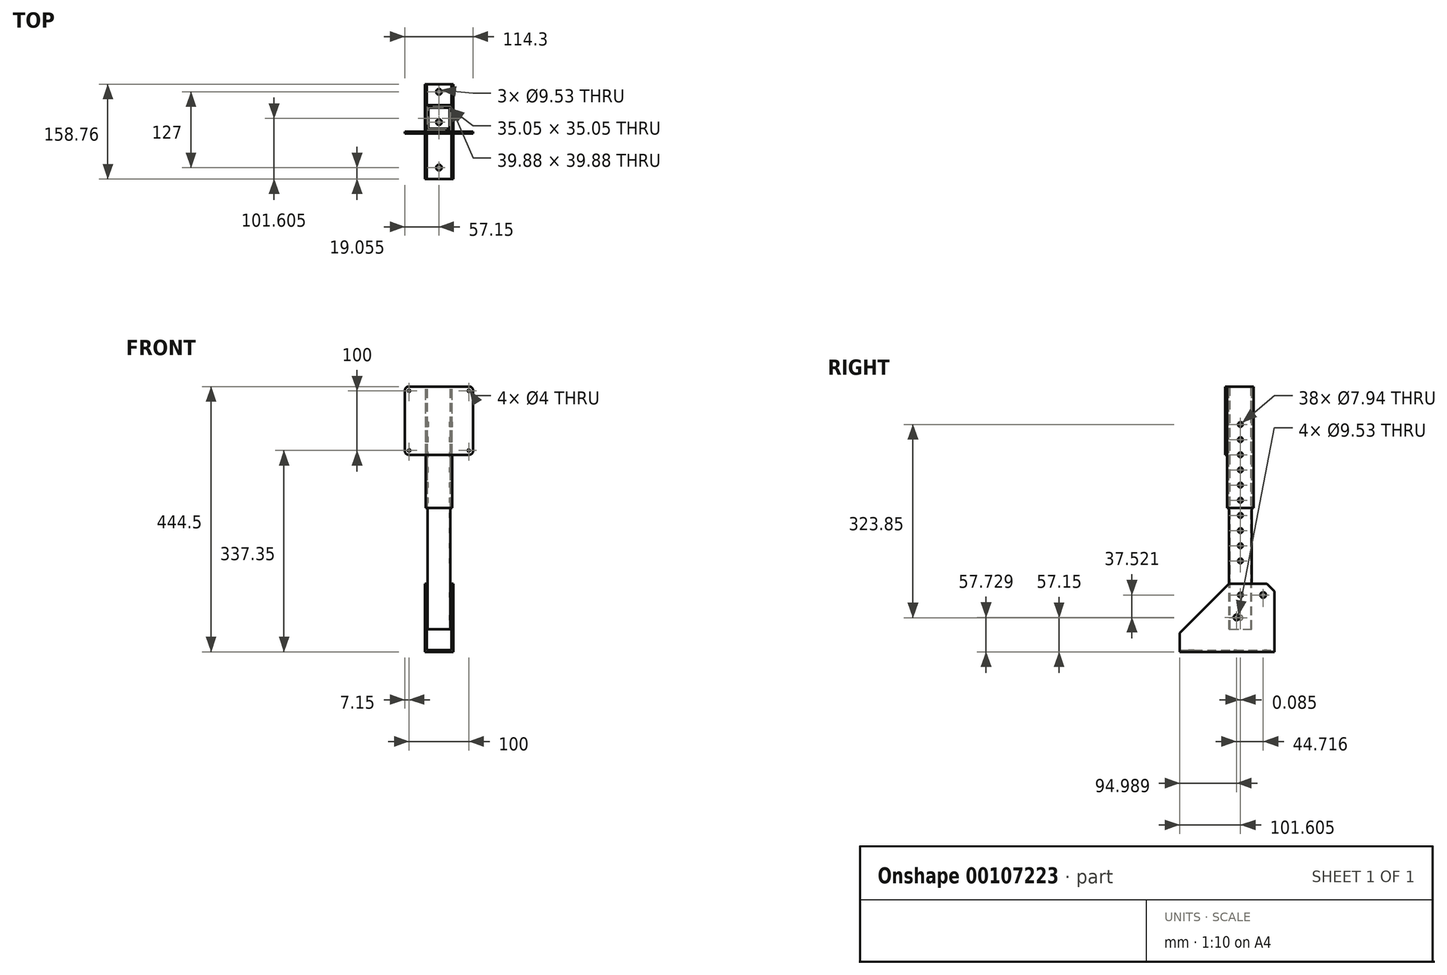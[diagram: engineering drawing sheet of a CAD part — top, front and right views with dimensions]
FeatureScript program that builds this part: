
annotation { "Feature Type Name" : "Feature", "Feature Type Description" : "" }
export const myFeature = defineFeature(function(context is Context, id is Id, definition is map)
    precondition{}
    {
        {
            var Q0;
            Q0=qCreatedBy(makeId("Front.planeOp"),FACE);
            var sketch = newSketch(context, id + "F0", { "sketchPlane" : qUnion([Q0])});
            skLineSegment(sketch, "E0.bottom", {"start": v(50, 50) * mm, "end": v(-50, 50) * mm, "construction": true});
            skLineSegment(sketch, "E0.top", {"start": v(50, -50) * mm, "end": v(-50, -50) * mm, "construction": true});
            skLineSegment(sketch, "E0.left", {"start": v(50, 50) * mm, "end": v(50, -50) * mm, "construction": true});
            skLineSegment(sketch, "E0.right", {"start": v(-50, 50) * mm, "end": v(-50, -50) * mm, "construction": true});
            skPoint(sketch, "E0.middle", {"position": v(0, 0) * mm});
            skCircle(sketch, "E1", {"center": v(-50, 50) * mm, "radius": 2 * mm});
            skCircle(sketch, "E2", {"center": v(50, 50) * mm, "radius": 2 * mm});
            skCircle(sketch, "E3", {"center": v(50, -50) * mm, "radius": 2 * mm});
            skCircle(sketch, "E4", {"center": v(-50, -50) * mm, "radius": 2 * mm});
            skLineSegment(sketch, "E5.bottom", {"start": v(57.15, 57.15) * mm, "end": v(-57.15, 57.15) * mm});
            skLineSegment(sketch, "E5.top", {"start": v(57.15, -57.15) * mm, "end": v(-57.15, -57.15) * mm});
            skLineSegment(sketch, "E5.left", {"start": v(57.15, 57.15) * mm, "end": v(57.15, -57.15) * mm});
            skLineSegment(sketch, "E5.right", {"start": v(-57.15, 57.15) * mm, "end": v(-57.15, -57.15) * mm});
            skSolve(sketch);
        }
        {
            var Q0;
            Q0=makeQuery(id+"F0.imprint","IMPRINT",FACE,{"disambiguationData":[TD([[makeQuery(id+"F0.imprint","IMPRINT",EDGE,{"derivedFrom":sQuery(id+"F0.wireOp",EDGE,"E1")}),-1.0]])]});
            extrude(context, id + "F1", {"entities" : qUnion([Q0]), "depth" : 3.17 * mm});
        }
        {
            var Q0;
            Q0=makeQuery(id+"F1.opExtrude","SWEPT_EDGE",EDGE,{"disambiguationData":[OSD([sQuery(id+"F0.wireOp",EDGE,"E5.bottom"),sQuery(id+"F0.wireOp",EDGE,"E5.right")])]});
            var Q1;
            Q1=makeQuery(id+"F1.opExtrude","SWEPT_EDGE",EDGE,{"disambiguationData":[OSD([sQuery(id+"F0.wireOp",EDGE,"E5.bottom"),sQuery(id+"F0.wireOp",EDGE,"E5.left")])]});
            var Q2;
            Q2=makeQuery(id+"F1.opExtrude","SWEPT_EDGE",EDGE,{"disambiguationData":[OSD([sQuery(id+"F0.wireOp",EDGE,"E5.top"),sQuery(id+"F0.wireOp",EDGE,"E5.right")])]});
            var Q3;
            Q3=makeQuery(id+"F1.opExtrude","SWEPT_EDGE",EDGE,{"disambiguationData":[OSD([sQuery(id+"F0.wireOp",EDGE,"E5.top"),sQuery(id+"F0.wireOp",EDGE,"E5.left")])]});
            fillet(context, id + "F2", {"entities" : qUnion([Q0, Q1, Q2, Q3]), "radius" : 6.35 * mm, "tangentPropagation" : true, "allowEdgeOverflow" : false});
        }
        {
            var Q0;
            Q0=makeQuery(id+"F1.opExtrude","SWEPT_FACE",FACE,{"disambiguationData":[OSD([sQuery(id+"F0.wireOp",EDGE,"E5.bottom")])]});
            var sketch = newSketch(context, id + "F3", { "sketchPlane" : qUnion([Q0])});
            skLineSegment(sketch, "E6.bottom", {"start": v(-22.23, 0) * mm, "end": v(22.23, 0) * mm});
            skLineSegment(sketch, "E6.top", {"start": v(-22.23, 44.45) * mm, "end": v(22.23, 44.45) * mm});
            skLineSegment(sketch, "E6.left", {"start": v(-22.23, 0) * mm, "end": v(-22.23, 44.45) * mm});
            skLineSegment(sketch, "E6.right", {"start": v(22.23, 0) * mm, "end": v(22.23, 44.45) * mm});
            skLineSegment(sketch, "E7.0", {"start": v(-19.94, 42.16) * mm, "end": v(19.94, 42.16) * mm});
            skLineSegment(sketch, "E7.1", {"start": v(-19.94, 2.29) * mm, "end": v(-19.94, 42.16) * mm});
            skLineSegment(sketch, "E7.2", {"start": v(-19.94, 2.29) * mm, "end": v(19.94, 2.29) * mm});
            skLineSegment(sketch, "E7.3", {"start": v(19.94, 2.29) * mm, "end": v(19.94, 42.16) * mm});
            skSolve(sketch);
        }
        {
            var Q0;
            Q0=makeQuery(id+"F3.imprint","IMPRINT",FACE,{"disambiguationData":[TD([[makeQuery(id+"F3.imprint","IMPRINT",EDGE,{"derivedFrom":sQuery(id+"F3.wireOp",EDGE,"E6.bottom")}),-1.0]])]});
            extrude(context, id + "F4", {"entities" : qUnion([Q0]), "oppositeDirection" : true, "depth" : 203.2 * mm});
        }
        {
            var Q0;
            Q0=qCreatedBy(makeId("Front.planeOp"),FACE);
            var sketch = newSketch(context, id + "F5", { "sketchPlane" : qUnion([Q0])});
            skLineSegment(sketch, "E8.bottom", {"start": v(-254, -155.95) * mm, "end": v(254, -155.95) * mm});
            skLineSegment(sketch, "E8.top", {"start": v(-254, 148.85) * mm, "end": v(254, 148.85) * mm});
            skLineSegment(sketch, "E8.left", {"start": v(-254, -155.95) * mm, "end": v(-254, 148.85) * mm});
            skLineSegment(sketch, "E8.right", {"start": v(254, -155.95) * mm, "end": v(254, 148.85) * mm});
            skLineSegment(sketch, "E9.bottom", {"start": v(-457.2, -384.55) * mm, "end": v(457.2, -384.55) * mm});
            skLineSegment(sketch, "E9.top", {"start": v(-457.2, -397.25) * mm, "end": v(457.2, -397.25) * mm});
            skLineSegment(sketch, "E9.left", {"start": v(-457.2, -384.55) * mm, "end": v(-457.2, -397.25) * mm});
            skLineSegment(sketch, "E9.right", {"start": v(457.2, -384.55) * mm, "end": v(457.2, -397.25) * mm});
            skLineSegment(sketch, "E10", {"start": v(0, -155.95) * mm, "end": v(0, -384.55) * mm});
            skSolve(sketch);
        }
        {
            var Q0;
            Q0=qCreatedBy(makeId("Right.planeOp"),FACE);
            var sketch = newSketch(context, id + "F6", { "sketchPlane" : qUnion([Q0])});
            skLineSegment(sketch, "E11.bottom", {"start": v(3.18, -387.35) * mm, "end": v(79.38, -387.35) * mm});
            skLineSegment(sketch, "E11.top", {"start": v(3.18, -273.05) * mm, "end": v(79.38, -273.05) * mm});
            skLineSegment(sketch, "E11.left", {"start": v(3.18, -387.35) * mm, "end": v(3.18, -273.05) * mm, "construction": true});
            skLineSegment(sketch, "E11.right", {"start": v(79.38, -387.35) * mm, "end": v(79.38, -273.05) * mm});
            skCircle(sketch, "E12", {"center": v(22.23, -292.1) * mm, "radius": 3.97 * mm});
            skCircle(sketch, "E13", {"center": v(15.6, -329.62) * mm, "radius": 4.76 * mm});
            skCircle(sketch, "E14", {"center": v(60.33, -292.1) * mm, "radius": 4.76 * mm});
            skLineSegment(sketch, "E15", {"start": v(22.23, -292.1) * mm, "end": v(60.33, -292.1) * mm, "construction": true});
            skLineSegment(sketch, "E16", {"start": v(15.6, -329.62) * mm, "end": v(22.23, -292.1) * mm, "construction": true});
            skLineSegment(sketch, "E17", {"start": v(3.18, -387.35) * mm, "end": v(-79.37, -387.35) * mm});
            skLineSegment(sketch, "E18", {"start": v(-79.37, -387.35) * mm, "end": v(-79.37, -355.6) * mm});
            skLineSegment(sketch, "E19", {"start": v(-79.37, -355.6) * mm, "end": v(3.18, -273.05) * mm});
            skSolve(sketch);
        }
        {
            var Q0;
            Q0=makeQuery(id+"F6.imprint","IMPRINT",FACE,{"disambiguationData":[TD([[makeQuery(id+"F6.imprint","IMPRINT",EDGE,{"derivedFrom":sQuery(id+"F6.wireOp",EDGE,"E11.bottom")}),1.0]])]});
            extrude(context, id + "F7", {"entities" : qUnion([Q0]), "endBound" : BoundingType.SYMMETRIC, "depth" : 47.62 * mm});
        }
        {
            var Q0;
            Q0=makeQuery(id+"F7.opExtrude","SWEPT_FACE",FACE,{"disambiguationData":[OSD([sQuery(id+"F6.wireOp",EDGE,"E11.right")])]});
            var Q1;
            Q1=makeQuery(id+"F7.opExtrude","SWEPT_FACE",FACE,{"disambiguationData":[OSD([sQuery(id+"F6.wireOp",EDGE,"E11.top")])]});
            var Q2;
            Q2=makeQuery(id+"F7.opExtrude","SWEPT_FACE",FACE,{"disambiguationData":[OSD([sQuery(id+"F6.wireOp",EDGE,"E13")])]});
            var Q3;
            Q3=makeQuery(id+"F7.opExtrude","SWEPT_FACE",FACE,{"disambiguationData":[OSD([sQuery(id+"F6.wireOp",EDGE,"E12")])]});
            var Q4;
            Q4=makeQuery(id+"F7.opExtrude","SWEPT_FACE",FACE,{"disambiguationData":[OSD([sQuery(id+"F6.wireOp",EDGE,"E14")])]});
            var Q5;
            Q5=makeQuery(id+"F7.opExtrude","SWEPT_FACE",FACE,{"disambiguationData":[OSD([sQuery(id+"F6.wireOp",EDGE,"E18")])]});
            var Q6;
            Q6=makeQuery(id+"F7.opExtrude","SWEPT_FACE",FACE,{"disambiguationData":[OSD([sQuery(id+"F6.wireOp",EDGE,"E19")])]});
            shell(context, id + "F8", {"entities" : qUnion([Q0, Q1, Q2, Q3, Q4, Q5, Q6]), "thickness" : 3.17 * mm});
        }
        {
            var Q0;
            Q0=qCreatedBy(makeId("Right.planeOp"),FACE);
            var sketch = newSketch(context, id + "F9", { "sketchPlane" : qUnion([Q0])});
            skLineSegment(sketch, "E20.bottom", {"start": v(3.18, -349.25) * mm, "end": v(41.28, -349.25) * mm});
            skLineSegment(sketch, "E20.top", {"start": v(3.17, 57.15) * mm, "end": v(41.27, 57.15) * mm});
            skLineSegment(sketch, "E20.left", {"start": v(3.18, -349.25) * mm, "end": v(3.17, 57.15) * mm});
            skLineSegment(sketch, "E20.right", {"start": v(41.28, -349.25) * mm, "end": v(41.27, 57.15) * mm});
            skCircle(sketch, "E21.0", {"center": v(22.23, -292.1) * mm, "radius": 3.97 * mm});
            skCircle(sketch, "E22", {"center": v(22.31, -330.2) * mm, "radius": 3.97 * mm});
            skLineSegment(sketch, "E23", {"start": v(22.31, -330.2) * mm, "end": v(22.23, -292.1) * mm, "construction": true});
            skSolve(sketch);
        }
        {
            var Q0;
            Q0=makeQuery(id+"F9.imprint","IMPRINT",FACE,{"disambiguationData":[TD([[makeQuery(id+"F9.imprint","IMPRINT",EDGE,{"derivedFrom":sQuery(id+"F9.wireOp",EDGE,"E20.bottom")}),1.0]])]});
            var Q1;
            Q1=sQuery(id+"F9.wireOp",EDGE,"E20.right");
            extrude(context, id + "F10", {"entities" : qUnion([Q0]), "surfaceEntities" : qUnion([Q1]), "endBound" : BoundingType.SYMMETRIC, "depth" : 38.1 * mm});
        }
        {
            var Q0;
            Q0=makeQuery(id+"F10.opExtrude","SWEPT_FACE",FACE,{"disambiguationData":[OSD([sQuery(id+"F9.wireOp",EDGE,"E20.top")])]});
            var Q1;
            Q1=makeQuery(id+"F10.opExtrude","SWEPT_FACE",FACE,{"disambiguationData":[OSD([sQuery(id+"F9.wireOp",EDGE,"E21.0")])]});
            var Q2;
            Q2=makeQuery(id+"F10.opExtrude","SWEPT_FACE",FACE,{"disambiguationData":[OSD([sQuery(id+"F9.wireOp",EDGE,"E20.bottom")])]});
            var Q3;
            Q3=makeQuery(id+"F10.opExtrude","SWEPT_FACE",FACE,{"disambiguationData":[OSD([sQuery(id+"F9.wireOp",EDGE,"E22")])]});
            shell(context, id + "F11", {"entities" : qUnion([Q0, Q1, Q2, Q3]), "thickness" : 1.52 * mm});
        }
        {
            var Q0;
            Q0=qCreatedBy(makeId("Right.planeOp"),FACE);
            var sketch = newSketch(context, id + "F12", { "sketchPlane" : qUnion([Q0])});
            skCircle(sketch, "E24", {"center": v(22.23, -133.35) * mm, "radius": 3.97 * mm});
            skLineSegment(sketch, "E25", {"start": v(22.23, -133.35) * mm, "end": v(22.23, -146.05) * mm, "construction": true});
            skLineSegment(sketch, "E26.0", {"start": v(0, -146.05) * mm, "end": v(44.45, -146.05) * mm, "construction": true});
            skSolve(sketch);
        }
        {
            var Q0;
            Q0 = qSketchRegion(id + "F12", true);
            extrude(context, id + "F13", {"entities" : qUnion([Q0]), "operationType" : NewBodyOperationType.REMOVE, "endBound" : BoundingType.SYMMETRIC, "oppositeDirection" : true, "depth" : 101.6 * mm});
        }
        {
            var Q0;
            Q0=makeQuery(id+"F10.opExtrude","CAP_FACE",FACE,{"disambiguationData":[OSD([sQuery(id+"F9.wireOp",EDGE,"E20.bottom"),sQuery(id+"F9.wireOp",EDGE,"E20.top"),sQuery(id+"F9.wireOp",EDGE,"E20.left"),sQuery(id+"F9.wireOp",EDGE,"E20.right"),sQuery(id+"F9.wireOp",EDGE,"E21.0"),sQuery(id+"F9.wireOp",EDGE,"E22")])],"isStart":false});
            var sketch = newSketch(context, id + "F14", { "sketchPlane" : qUnion([Q0])});
            skCircle(sketch, "E27", {"center": v(22.23, -6.35) * mm, "radius": 3.97 * mm});
            skLineSegment(sketch, "E28", {"start": v(22.23, -133.35) * mm, "end": v(22.23, -6.35) * mm, "construction": true});
            skCircle(sketch, "E29.0.1.0", {"center": v(22.23, -31.75) * mm, "radius": 3.97 * mm});
            skCircle(sketch, "E29.0.2.0", {"center": v(22.23, -57.15) * mm, "radius": 3.97 * mm});
            skCircle(sketch, "E29.0.3.0", {"center": v(22.23, -82.55) * mm, "radius": 3.97 * mm});
            skCircle(sketch, "E29.0.4.0", {"center": v(22.23, -107.95) * mm, "radius": 3.97 * mm});
            skCircle(sketch, "E29.0.5.0", {"center": v(22.23, -133.35) * mm, "radius": 3.97 * mm});
            skLineSegment(sketch, "E29.direction1", {"start": v(22.23, -6.35) * mm, "end": v(47.62, -6.35) * mm, "construction": true});
            skLineSegment(sketch, "E29.direction2", {"start": v(22.23, -6.35) * mm, "end": v(22.23, -31.75) * mm, "construction": true});
            skCircle(sketch, "E30.0.0.6", {"center": v(22.23, -158.75) * mm, "radius": 3.97 * mm});
            skCircle(sketch, "E30.0.0.7", {"center": v(22.23, -184.15) * mm, "radius": 3.97 * mm});
            skCircle(sketch, "E30.0.0.8", {"center": v(22.23, -209.55) * mm, "radius": 3.97 * mm});
            skCircle(sketch, "E30.0.0.9", {"center": v(22.23, -234.95) * mm, "radius": 3.97 * mm});
            skSolve(sketch);
        }
        {
            var Q0;
            Q0 = qSketchRegion(id + "F14", true);
            extrude(context, id + "F15", {"entities" : qUnion([Q0]), "operationType" : NewBodyOperationType.REMOVE, "endBound" : BoundingType.SYMMETRIC, "depth" : 101.6 * mm});
        }
        {
            var Q0;
            Q0=makeQuery(id+"F7.opExtrude","SWEPT_FACE",FACE,{"disambiguationData":[OSD([sQuery(id+"F6.wireOp",EDGE,"E11.bottom")])]});
            var sketch = newSketch(context, id + "F16", { "sketchPlane" : qUnion([Q0])});
            skCircle(sketch, "E31", {"center": v(0, -15.88) * mm, "radius": 4.76 * mm});
            skCircle(sketch, "E32", {"center": v(0, -66.68) * mm, "radius": 4.76 * mm});
            skSolve(sketch);
        }
        {
            var Q0;
            Q0 = qSketchRegion(id + "F16", true);
            extrude(context, id + "F17", {"entities" : qUnion([Q0]), "operationType" : NewBodyOperationType.REMOVE, "oppositeDirection" : true, "depth" : 25.4 * mm});
        }
        {
            var Q0;
            Q0=makeQuery(id+"F8.opShell","OFFSET_FACE",FACE,{"disambiguationData":[OSD([sQuery(id+"F6.wireOp",EDGE,"E11.bottom"),sQuery(id+"F6.wireOp",EDGE,"E17")])]});
            var sketch = newSketch(context, id + "F18", { "sketchPlane" : qUnion([Q0])});
            skCircle(sketch, "E33", {"center": v(0, -60.32) * mm, "radius": 4.76 * mm});
            skSolve(sketch);
        }
        {
            var Q0;
            Q0=makeQuery(id+"F18.imprint","IMPRINT",FACE,{"disambiguationData":[TD([[makeQuery(id+"F18.imprint","IMPRINT",EDGE,{"derivedFrom":sQuery(id+"F18.wireOp",EDGE,"E33")}),1.0]])]});
            extrude(context, id + "F19", {"entities" : qUnion([Q0]), "operationType" : NewBodyOperationType.REMOVE, "oppositeDirection" : true, "depth" : 25.4 * mm});
        }
        {
            var Q0;
            Q0=makeQuery(id+"F7.opExtrude","SWEPT_EDGE",EDGE,{"disambiguationData":[OSD([sQuery(id+"F6.wireOp",EDGE,"E11.top"),sQuery(id+"F6.wireOp",EDGE,"E11.right")])]});
            var Q1;
            Q1=makeQuery(id+"F8.opShell","OFFSET_EDGE",EDGE,{"disambiguationData":[OSD([sQuery(id+"F6.wireOp",EDGE,"E11.top"),sQuery(id+"F6.wireOp",EDGE,"E11.right")])]});
            chamfer(context, id + "F20", {"entities" : qUnion([Q0, Q1]), "width" : 12.7 * mm, "tangentPropagation" : true});
        }
    });
